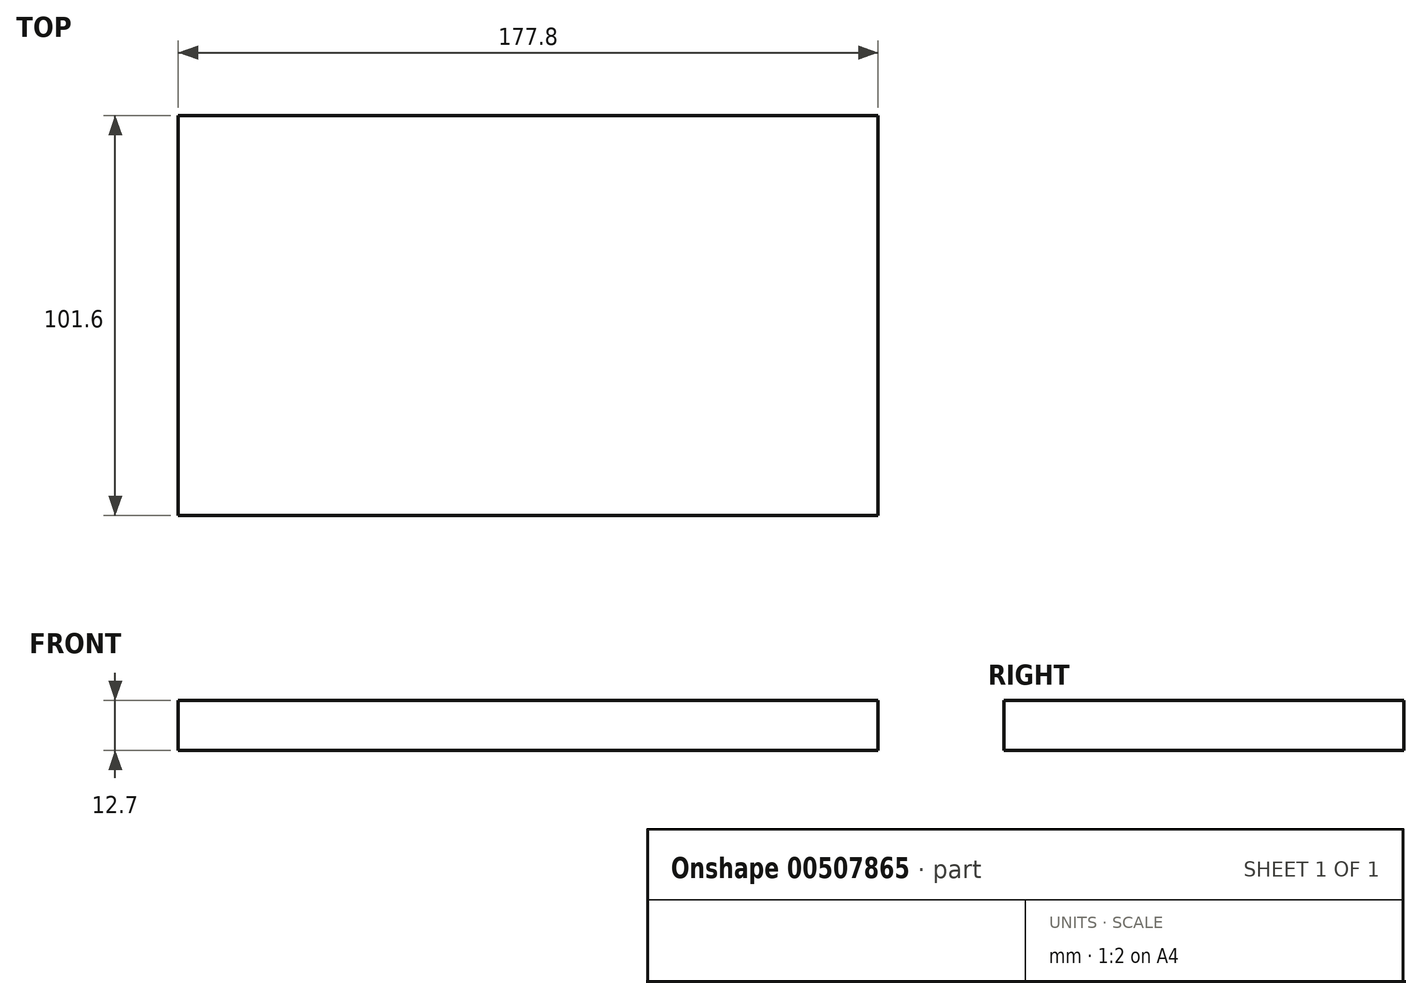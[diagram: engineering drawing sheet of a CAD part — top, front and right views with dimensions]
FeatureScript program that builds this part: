
annotation { "Feature Type Name" : "Feature", "Feature Type Description" : "" }
export const myFeature = defineFeature(function(context is Context, id is Id, definition is map)
    precondition{}
    {
        {
            var Q0;
            Q0=qCreatedBy(makeId("Top.planeOp"),FACE);
            var sketch = newSketch(context, id + "F0", { "sketchPlane" : qUnion([Q0])});
            skLineSegment(sketch, "E0.bottom", {"start": v(-88.9, 50.8) * mm, "end": v(88.9, 50.8) * mm});
            skLineSegment(sketch, "E0.top", {"start": v(-88.9, -50.8) * mm, "end": v(88.9, -50.8) * mm});
            skLineSegment(sketch, "E0.left", {"start": v(-88.9, 50.8) * mm, "end": v(-88.9, -50.8) * mm});
            skLineSegment(sketch, "E0.right", {"start": v(88.9, 50.8) * mm, "end": v(88.9, -50.8) * mm});
            skPoint(sketch, "E0.middle", {"position": v(0, 0) * mm});
            skSolve(sketch);
        }
        {
            var Q0;
            Q0 = qSketchRegion(id + "F0", true);
            extrude(context, id + "F1", {"entities" : qUnion([Q0]), "depth" : 12.7 * mm, "offsetDistance" : 25.4 * mm});
        }
    });
